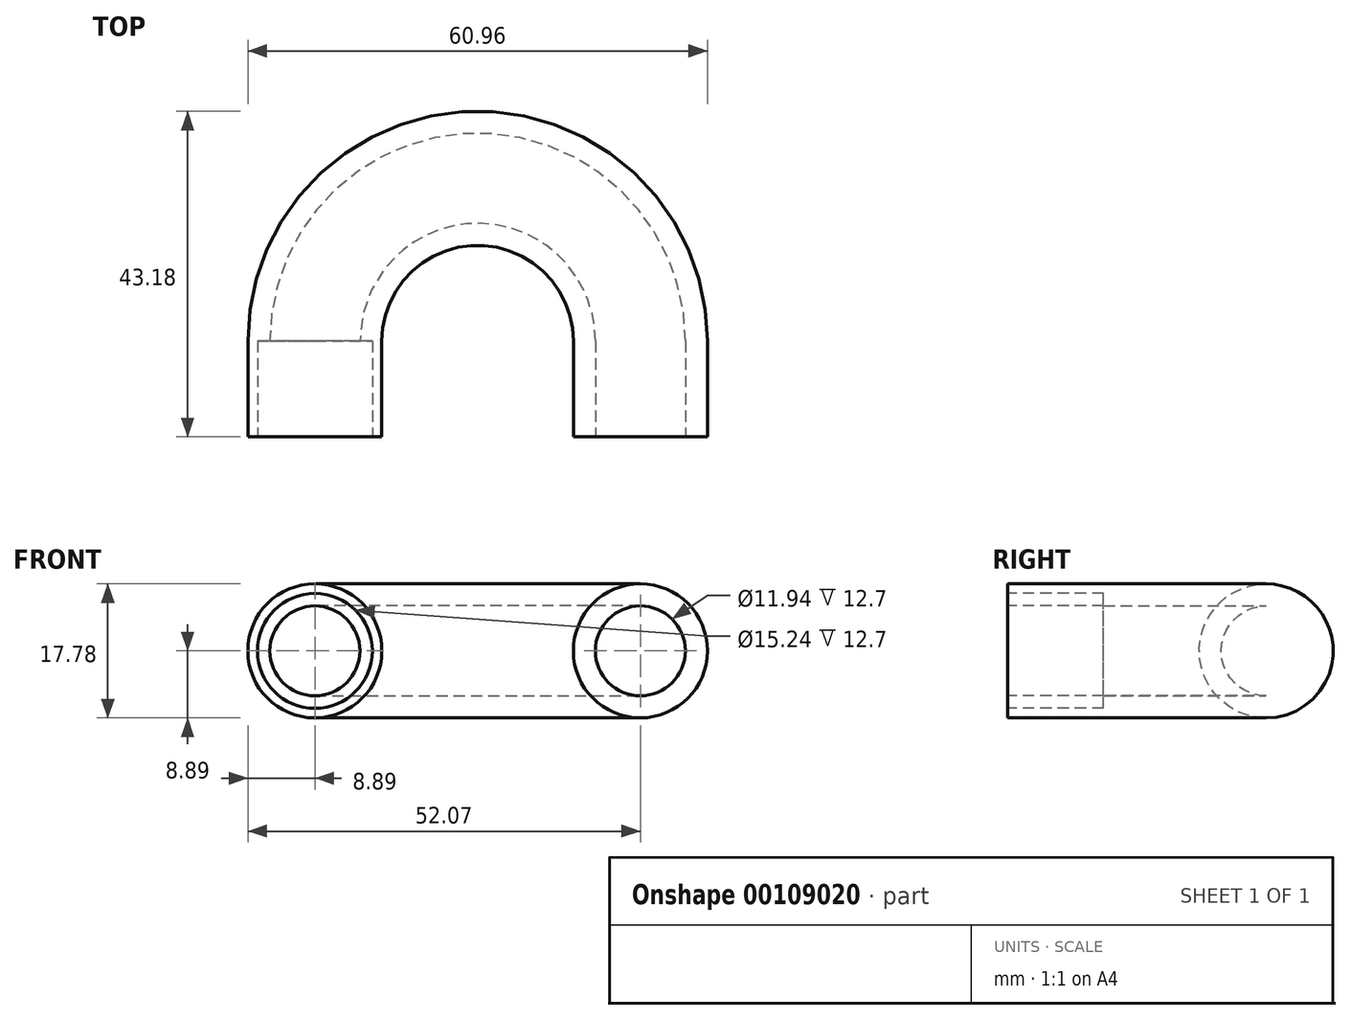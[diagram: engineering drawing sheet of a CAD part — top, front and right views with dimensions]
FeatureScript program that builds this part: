
annotation { "Feature Type Name" : "Feature", "Feature Type Description" : "" }
export const myFeature = defineFeature(function(context is Context, id is Id, definition is map)
    precondition{}
    {
        {
            var Q0;
            Q0=qCreatedBy(makeId("Top.planeOp"),FACE);
            var sketch = newSketch(context, id + "F0", { "sketchPlane" : qUnion([Q0])});
            skLineSegment(sketch, "E0", {"start": v(0, 0) * mm, "end": v(0, 12.7) * mm});
            skArc(sketch, "E1", {"start": v(0, 12.7) * mm, "mid": v(21.59, 34.3) * mm, "end": v(43.18, 12.7) * mm});
            skLineSegment(sketch, "E2", {"start": v(43.18, 12.7) * mm, "end": v(43.18, 0) * mm});
            skSolve(sketch);
        }
        {
            var Q0;
            Q0=qCreatedBy(makeId("Front.planeOp"),FACE);
            var sketch = newSketch(context, id + "F1", { "sketchPlane" : qUnion([Q0])});
            skCircle(sketch, "E3", {"center": v(0, 0) * mm, "radius": 5.97 * mm});
            skCircle(sketch, "E4", {"center": v(0, 0) * mm, "radius": 8.9 * mm});
            skSolve(sketch);
        }
        {
            var Q0;
            Q0=makeQuery(id+"F1.imprint","IMPRINT",FACE,{"disambiguationData":[TD([[makeQuery(id+"F1.imprint","IMPRINT",EDGE,{"derivedFrom":sQuery(id+"F1.wireOp",EDGE,"E3")}),-1.0]])]});
            var Q1;
            Q1=sQuery(id+"F0.wireOp",EDGE,"E0");
            var Q2;
            Q2=sQuery(id+"F0.wireOp",EDGE,"E1");
            var Q3;
            Q3=sQuery(id+"F0.wireOp",EDGE,"E2");
            sweep(context, id + "F2", {"profiles" : qUnion([Q0]), "path" : qUnion([Q1, Q2, Q3])});
        }
        {
            var Q0;
            Q0=makeQuery(id+"F2.opSweep","CAP_FACE",FACE,{"disambiguationData":[OSD([sQuery(id+"F0.wireOp",VERTEX,"E0.start"),sQuery(id+"F1.wireOp",EDGE,"E3"),sQuery(id+"F1.wireOp",EDGE,"E4")])],"isStart":true});
            var sketch = newSketch(context, id + "F3", { "sketchPlane" : qUnion([Q0])});
            skCircle(sketch, "E5", {"center": v(0, 0) * mm, "radius": 7.62 * mm});
            skSolve(sketch);
        }
        {
            var Q0;
            Q0=makeQuery(id+"F3.imprint","IMPRINT",FACE,{"disambiguationData":[TD([[makeQuery(id+"F3.imprint","IMPRINT",EDGE,{"derivedFrom":sQuery(id+"F3.wireOp",EDGE,"E5")}),1.0]])]});
            extrude(context, id + "F4", {"entities" : qUnion([Q0]), "operationType" : NewBodyOperationType.REMOVE, "oppositeDirection" : true, "depth" : 12.7 * mm});
        }
    });
